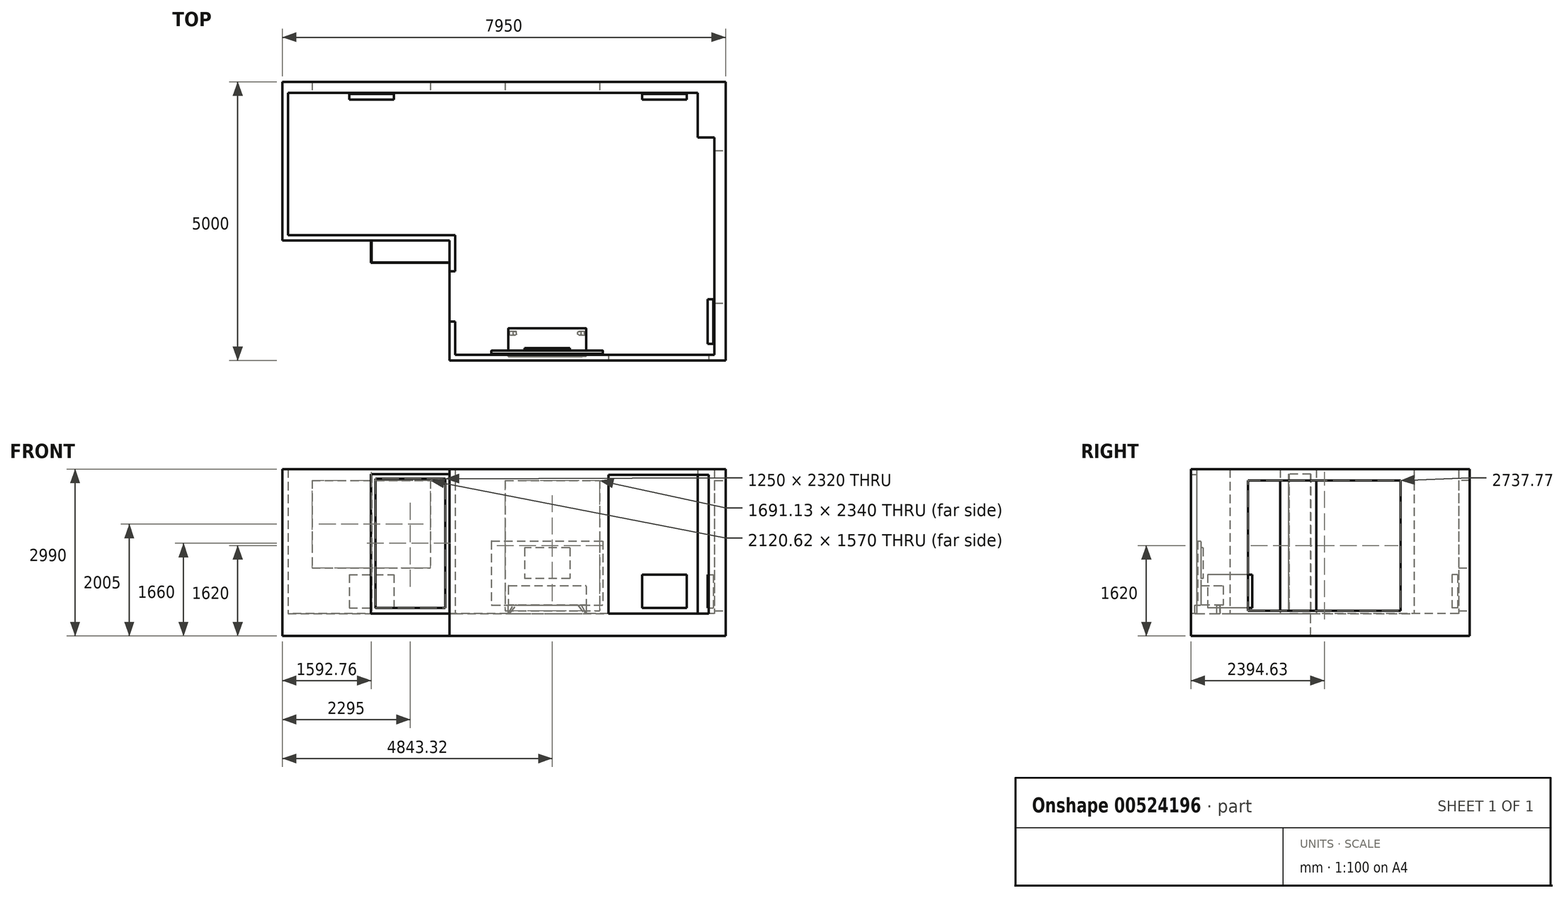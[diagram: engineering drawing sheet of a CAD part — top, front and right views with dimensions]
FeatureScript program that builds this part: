
annotation { "Feature Type Name" : "Feature", "Feature Type Description" : "" }
export const myFeature = defineFeature(function(context is Context, id is Id, definition is map)
    precondition{}
    {
        {
            var Q0;
            Q0=qCreatedBy(makeId("Top.planeOp"),FACE);
            var sketch = newSketch(context, id + "F0", { "sketchPlane" : qUnion([Q0])});
            skLineSegment(sketch, "E0.bottom", {"start": v(0, 0) * mm, "end": v(-4650, 0) * mm});
            skLineSegment(sketch, "E0.left", {"start": v(0, 0) * mm, "end": v(0, 3900) * mm});
            skLineSegment(sketch, "E0.right", {"start": v(-4650, 0) * mm, "end": v(-4650, 2150) * mm});
            skLineSegment(sketch, "E1.top", {"start": v(-4650, 2150) * mm, "end": v(-7650, 2150) * mm});
            skLineSegment(sketch, "E1.right", {"start": v(-7650, 4700) * mm, "end": v(-7650, 2150) * mm});
            skLineSegment(sketch, "E2", {"start": v(-7650, 4700) * mm, "end": v(-300, 4700) * mm});
            skLineSegment(sketch, "E3.bottom", {"start": v(-7750, 4900) * mm, "end": v(200, 4900) * mm});
            skLineSegment(sketch, "E3.top", {"start": v(-4750, -100) * mm, "end": v(200, -100) * mm});
            skLineSegment(sketch, "E3.left", {"start": v(-7750, 4900) * mm, "end": v(-7750, 2050) * mm});
            skLineSegment(sketch, "E3.right", {"start": v(200, 4900) * mm, "end": v(200, -100) * mm});
            skLineSegment(sketch, "E4.top", {"start": v(-7750, 2050) * mm, "end": v(-4750, 2050) * mm});
            skLineSegment(sketch, "E4.right", {"start": v(-4750, -100) * mm, "end": v(-4750, 2050) * mm});
            skLineSegment(sketch, "E5.bottom", {"start": v(-1900, 0) * mm, "end": v(-100, 0) * mm});
            skLineSegment(sketch, "E5.top", {"start": v(-1900, -100) * mm, "end": v(-100, -100) * mm});
            skLineSegment(sketch, "E5.left", {"start": v(-1900, 0) * mm, "end": v(-1900, -100) * mm});
            skLineSegment(sketch, "E5.right", {"start": v(-100, 0) * mm, "end": v(-100, -100) * mm});
            skLineSegment(sketch, "E6.bottom", {"start": v(-4750, 1500) * mm, "end": v(-4650, 1500) * mm});
            skLineSegment(sketch, "E6.top", {"start": v(-4750, 600) * mm, "end": v(-4650, 600) * mm});
            skLineSegment(sketch, "E6.left", {"start": v(-4750, 1500) * mm, "end": v(-4750, 600) * mm});
            skLineSegment(sketch, "E6.right", {"start": v(-4650, 1500) * mm, "end": v(-4650, 600) * mm});
            skLineSegment(sketch, "E7.bottom", {"start": v(-6160, 2050) * mm, "end": v(-4750, 2050) * mm});
            skLineSegment(sketch, "E7.top", {"start": v(-6160, 1650) * mm, "end": v(-4750, 1650) * mm});
            skLineSegment(sketch, "E7.left", {"start": v(-6160, 2050) * mm, "end": v(-6160, 1650) * mm});
            skLineSegment(sketch, "E7.right", {"start": v(-4750, 2050) * mm, "end": v(-4750, 1650) * mm});
            skLineSegment(sketch, "E8.bottom", {"start": v(-6150, 2050) * mm, "end": v(-4750, 2050) * mm});
            skLineSegment(sketch, "E8.top", {"start": v(-6150, 1660) * mm, "end": v(-4750, 1660) * mm});
            skLineSegment(sketch, "E8.left", {"start": v(-6150, 2050) * mm, "end": v(-6150, 1660) * mm});
            skLineSegment(sketch, "E8.right", {"start": v(-4750, 2050) * mm, "end": v(-4750, 1660) * mm});
            skLineSegment(sketch, "E9.top", {"start": v(-300, 3900) * mm, "end": v(0, 3900) * mm});
            skLineSegment(sketch, "E9.left", {"start": v(-300, 4700) * mm, "end": v(-300, 3900) * mm});
            skPoint(sketch, "E10.orphan", {"position": v(0, 4700) * mm});
            skLineSegment(sketch, "E11.bottom", {"start": v(0, 3663.51) * mm, "end": v(200, 3663.51) * mm});
            skLineSegment(sketch, "E11.top", {"start": v(0, 925.75) * mm, "end": v(200, 925.75) * mm});
            skLineSegment(sketch, "E11.left", {"start": v(0, 3663.51) * mm, "end": v(0, 925.75) * mm});
            skLineSegment(sketch, "E11.right", {"start": v(200, 3663.51) * mm, "end": v(200, 925.75) * mm});
            skLineSegment(sketch, "E12.bottom", {"start": v(-3752.24, 4700) * mm, "end": v(-2061.12, 4700) * mm});
            skLineSegment(sketch, "E12.top", {"start": v(-3752.24, 4900) * mm, "end": v(-2061.12, 4900) * mm});
            skLineSegment(sketch, "E12.left", {"start": v(-3752.24, 4700) * mm, "end": v(-3752.24, 4900) * mm});
            skLineSegment(sketch, "E12.right", {"start": v(-2061.12, 4700) * mm, "end": v(-2061.12, 4900) * mm});
            skLineSegment(sketch, "E13.bottom", {"start": v(-7217.55, 4700) * mm, "end": v(-5096.93, 4700) * mm});
            skLineSegment(sketch, "E13.top", {"start": v(-7217.55, 4900) * mm, "end": v(-5096.93, 4900) * mm});
            skLineSegment(sketch, "E13.left", {"start": v(-7217.55, 4700) * mm, "end": v(-7217.55, 4900) * mm});
            skLineSegment(sketch, "E13.right", {"start": v(-5096.93, 4700) * mm, "end": v(-5096.93, 4900) * mm});
            skSolve(sketch);
        }
        {
            var Q0;
            {var subQ7=sQuery(id+"F0.wireOp",EDGE,"E1.top");Q0=makeQuery(id+"F0.imprint","IMPRINT",FACE,{"disambiguationData":[TD([[makeQuery(id+"F0.imprint","IMPRINT",EDGE,{"derivedFrom":subQ7}),1.0]])]});}
            var Q1;
            {var subQ0=sQuery(id+"F0.wireOp",EDGE,"E1.top");Q1=makeQuery(id+"F0.imprint","IMPRINT",FACE,{"disambiguationData":[TD([[makeQuery(id+"F0.imprint","IMPRINT",EDGE,{"derivedFrom":subQ0}),-1.0]])]});}
            var Q2;
            {var subQ2=sQuery(id+"F0.wireOp",EDGE,"E6.bottom");Q2=makeQuery(id+"F0.imprint","IMPRINT",FACE,{"disambiguationData":[TD([[makeQuery(id+"F0.imprint","IMPRINT",EDGE,{"derivedFrom":subQ2}),-1.0]])]});}
            var Q3;
            {var subQ4=sQuery(id+"F0.wireOp",EDGE,"E5.left");Q3=makeQuery(id+"F0.imprint","IMPRINT",FACE,{"disambiguationData":[TD([[makeQuery(id+"F0.imprint","IMPRINT",EDGE,{"derivedFrom":subQ4}),-1.0]])]});}
            var Q4;
            {var subQ0=sQuery(id+"F0.wireOp",EDGE,"E12.left");Q4=makeQuery(id+"F0.imprint","IMPRINT",FACE,{"disambiguationData":[TD([[makeQuery(id+"F0.imprint","IMPRINT",EDGE,{"derivedFrom":subQ0}),-1.0]])]});}
            var Q5;
            {var subQ5=sQuery(id+"F0.wireOp",EDGE,"E9.top");Q5=makeQuery(id+"F0.imprint","IMPRINT",FACE,{"disambiguationData":[TD([[makeQuery(id+"F0.imprint","IMPRINT",EDGE,{"derivedFrom":subQ5}),1.0]])]});}
            var Q6;
            {var subQ0=sQuery(id+"F0.wireOp",EDGE,"E13.left");Q6=makeQuery(id+"F0.imprint","IMPRINT",FACE,{"disambiguationData":[TD([[makeQuery(id+"F0.imprint","IMPRINT",EDGE,{"derivedFrom":subQ0}),-1.0]])]});}
            var Q7;
            {var subQ0=sQuery(id+"F0.wireOp",EDGE,"E12.left");Q7=makeQuery(id+"F0.imprint","IMPRINT",FACE,{"disambiguationData":[TD([[makeQuery(id+"F0.imprint","IMPRINT",EDGE,{"derivedFrom":subQ0}),1.0]])]});}
            var Q8;
            {var subQ2=sQuery(id+"F0.wireOp",EDGE,"E11.bottom");Q8=makeQuery(id+"F0.imprint","IMPRINT",FACE,{"disambiguationData":[TD([[makeQuery(id+"F0.imprint","IMPRINT",EDGE,{"derivedFrom":subQ2}),-1.0]])]});}
            var Q9;
            {var subQ3=sQuery(id+"F0.wireOp",EDGE,"E5.right");Q9=makeQuery(id+"F0.imprint","IMPRINT",FACE,{"disambiguationData":[TD([[makeQuery(id+"F0.imprint","IMPRINT",EDGE,{"derivedFrom":subQ3}),1.0]])]});}
            var Q10;
            {var subQ0=sQuery(id+"F0.wireOp",EDGE,"E5.left");Q10=makeQuery(id+"F0.imprint","IMPRINT",FACE,{"disambiguationData":[TD([[makeQuery(id+"F0.imprint","IMPRINT",EDGE,{"derivedFrom":subQ0}),1.0]])]});}
            extrude(context, id + "F1", {"entities" : qUnion([Q0, Q1, Q2, Q3, Q4, Q5, Q6, Q7, Q8, Q9, Q10]), "oppositeDirection" : true, "depth" : 400 * mm, "offsetDistance" : 25 * mm});
        }
        {
            var Q0;
            {var subQ7=sQuery(id+"F0.wireOp",EDGE,"E1.top");Q0=makeQuery(id+"F0.imprint","IMPRINT",FACE,{"disambiguationData":[TD([[makeQuery(id+"F0.imprint","IMPRINT",EDGE,{"derivedFrom":subQ7}),1.0]])]});}
            var Q1;
            {var subQ0=sQuery(id+"F0.wireOp",EDGE,"E12.left");Q1=makeQuery(id+"F0.imprint","IMPRINT",FACE,{"disambiguationData":[TD([[makeQuery(id+"F0.imprint","IMPRINT",EDGE,{"derivedFrom":subQ0}),1.0]])]});}
            var Q2;
            {var subQ5=sQuery(id+"F0.wireOp",EDGE,"E9.top");Q2=makeQuery(id+"F0.imprint","IMPRINT",FACE,{"disambiguationData":[TD([[makeQuery(id+"F0.imprint","IMPRINT",EDGE,{"derivedFrom":subQ5}),1.0]])]});}
            var Q3;
            {var subQ3=sQuery(id+"F0.wireOp",EDGE,"E5.right");Q3=makeQuery(id+"F0.imprint","IMPRINT",FACE,{"disambiguationData":[TD([[makeQuery(id+"F0.imprint","IMPRINT",EDGE,{"derivedFrom":subQ3}),1.0]])]});}
            var Q4;
            {var subQ4=sQuery(id+"F0.wireOp",EDGE,"E5.left");Q4=makeQuery(id+"F0.imprint","IMPRINT",FACE,{"disambiguationData":[TD([[makeQuery(id+"F0.imprint","IMPRINT",EDGE,{"derivedFrom":subQ4}),-1.0]])]});}
            extrude(context, id + "F2", {"entities" : qUnion([Q0, Q1, Q2, Q3, Q4]), "operationType" : NewBodyOperationType.ADD, "depth" : 2590 * mm, "offsetDistance" : 25 * mm});
        }
        {
            var Q0;
            {var subQ0=sQuery(id+"F0.wireOp",EDGE,"E12.left");Q0=makeQuery(id+"F0.imprint","IMPRINT",FACE,{"disambiguationData":[TD([[makeQuery(id+"F0.imprint","IMPRINT",EDGE,{"derivedFrom":subQ0}),-1.0]])]});}
            var Q1;
            {var subQ2=sQuery(id+"F0.wireOp",EDGE,"E11.bottom");Q1=makeQuery(id+"F0.imprint","IMPRINT",FACE,{"disambiguationData":[TD([[makeQuery(id+"F0.imprint","IMPRINT",EDGE,{"derivedFrom":subQ2}),-1.0]])]});}
            extrude(context, id + "F3", {"entities" : qUnion([Q0, Q1]), "operationType" : NewBodyOperationType.ADD, "depth" : 50 * mm, "offsetDistance" : 25 * mm});
        }
        {
            var Q0;
            {var subQ0=sQuery(id+"F0.wireOp",EDGE,"E13.left");Q0=makeQuery(id+"F0.imprint","IMPRINT",FACE,{"disambiguationData":[TD([[makeQuery(id+"F0.imprint","IMPRINT",EDGE,{"derivedFrom":subQ0}),-1.0]])]});}
            extrude(context, id + "F4", {"entities" : qUnion([Q0]), "operationType" : NewBodyOperationType.ADD, "depth" : 820 * mm, "offsetDistance" : 25 * mm});
        }
        {
            var Q0;
            {var subQ3=sQuery(id+"F0.wireOp",EDGE,"E7.top");Q0=makeQuery(id+"F0.imprint","IMPRINT",FACE,{"disambiguationData":[TD([[makeQuery(id+"F0.imprint","IMPRINT",EDGE,{"derivedFrom":subQ3}),1.0]])]});}
            extrude(context, id + "F5", {"entities" : qUnion([Q0]), "operationType" : NewBodyOperationType.ADD, "depth" : 2500 * mm, "offsetDistance" : 25 * mm});
        }
        {
            var Q0;
            Q0=makeQuery(id+"F5.opExtrude","SWEPT_FACE",FACE,{"disambiguationData":[OSD([sQuery(id+"F0.wireOp",EDGE,"E7.top")])]});
            var sketch = newSketch(context, id + "F6", { "sketchPlane" : qUnion([Q0])});
            skLineSegment(sketch, "E14.0.0", {"start": v(-6160, 0) * mm, "end": v(-4750, 0) * mm});
            skLineSegment(sketch, "E14.0.1", {"start": v(-4750, 0) * mm, "end": v(-4750, 2500) * mm});
            skLineSegment(sketch, "E14.0.2", {"start": v(-4750, 2500) * mm, "end": v(-6160, 2500) * mm});
            skLineSegment(sketch, "E14.0.3", {"start": v(-6160, 2500) * mm, "end": v(-6160, 0) * mm});
            skLineSegment(sketch, "E15.bottom", {"start": v(-6080, 2420) * mm, "end": v(-4830, 2420) * mm});
            skLineSegment(sketch, "E15.top", {"start": v(-6080, 100) * mm, "end": v(-4830, 100) * mm});
            skLineSegment(sketch, "E15.left", {"start": v(-6080, 2420) * mm, "end": v(-6080, 100) * mm});
            skLineSegment(sketch, "E15.right", {"start": v(-4830, 2420) * mm, "end": v(-4830, 100) * mm});
            skSolve(sketch);
        }
        {
            var Q0;
            Q0=makeQuery(id+"F6.imprint","IMPRINT",FACE,{"disambiguationData":[TD([[makeQuery(id+"F6.imprint","IMPRINT",EDGE,{"derivedFrom":sQuery(id+"F6.wireOp",EDGE,"E15.bottom")}),-1.0]])]});
            extrude(context, id + "F7", {"entities" : qUnion([Q0]), "operationType" : NewBodyOperationType.REMOVE, "oppositeDirection" : true, "depth" : 25 * mm, "offsetDistance" : 25 * mm});
        }
        {
            var Q0;
            {var subQ0=sQuery(id+"F0.wireOp",EDGE,"E2");Q0=makeQuery(id+"F4.boolean.opBoolean","MERGE",FACE,{"derivedFrom":[makeQuery(id+"F2.opExtrude","SWEPT_FACE",FACE,{"disambiguationData":[OSD([subQ0]),TDD([makeQuery(id+"F0.imprint","IMPRINT",EDGE,{"disambiguationData":[TD([[makeQuery(id+"F0.imprint","INTERSECT",VERTEX,{"derivedFrom":[sQuery(id+"F0.wireOp",EDGE,"E1.right"),subQ0]}),-1.0]])],"derivedFrom":subQ0})])]}),makeQuery(id+"F3.boolean.opBoolean","MERGE",FACE,{"derivedFrom":[makeQuery(id+"F2.opExtrude","SWEPT_FACE",FACE,{"disambiguationData":[OSD([subQ0]),TDD([makeQuery(id+"F0.imprint","IMPRINT",EDGE,{"disambiguationData":[TD([[makeQuery(id+"F0.imprint","INTERSECT",VERTEX,{"derivedFrom":[subQ0,sQuery(id+"F0.wireOp",EDGE,"E9.left")]}),1.0]])],"derivedFrom":subQ0})])]}),makeQuery(id+"F2.opExtrude","SWEPT_FACE",FACE,{"disambiguationData":[OSD([subQ0]),TDD([makeQuery(id+"F0.imprint","IMPRINT",EDGE,{"disambiguationData":[TD([[makeQuery(id+"F0.imprint","INTERSECT",VERTEX,{"derivedFrom":[subQ0,sQuery(id+"F0.wireOp",EDGE,"E12.left")]}),1.0]])],"derivedFrom":subQ0})])]}),makeQuery(id+"F3.opExtrude","SWEPT_FACE",FACE,{"disambiguationData":[OSD([subQ0])]})]}),makeQuery(id+"F4.opExtrude","SWEPT_FACE",FACE,{"disambiguationData":[OSD([subQ0])]})]});}
            var sketch = newSketch(context, id + "F8", { "sketchPlane" : qUnion([Q0])});
            skLineSegment(sketch, "E16.0.0", {"start": v(-7650, 0) * mm, "end": v(-300, 0) * mm});
            skLineSegment(sketch, "E16.0.1", {"start": v(-300, 0) * mm, "end": v(-300, 2590) * mm});
            skLineSegment(sketch, "E16.0.2", {"start": v(-300, 2590) * mm, "end": v(-2061.12, 2590) * mm});
            skLineSegment(sketch, "E16.0.3", {"start": v(-2061.12, 2590) * mm, "end": v(-2061.12, 50) * mm});
            skLineSegment(sketch, "E16.0.4", {"start": v(-2061.12, 50) * mm, "end": v(-3752.24, 50) * mm});
            skLineSegment(sketch, "E16.0.5", {"start": v(-3752.24, 50) * mm, "end": v(-3752.24, 2590) * mm});
            skLineSegment(sketch, "E16.0.6", {"start": v(-3752.24, 2590) * mm, "end": v(-5096.93, 2590) * mm});
            skLineSegment(sketch, "E16.0.7", {"start": v(-5096.93, 2590) * mm, "end": v(-5096.93, 820) * mm});
            skLineSegment(sketch, "E16.0.8", {"start": v(-5096.93, 820) * mm, "end": v(-7217.55, 820) * mm});
            skLineSegment(sketch, "E16.0.9", {"start": v(-7217.55, 820) * mm, "end": v(-7217.55, 2590) * mm});
            skLineSegment(sketch, "E16.0.10", {"start": v(-7217.55, 2590) * mm, "end": v(-7650, 2590) * mm});
            skLineSegment(sketch, "E16.0.11", {"start": v(-7650, 2590) * mm, "end": v(-7650, 0) * mm});
            skLineSegment(sketch, "E17.bottom", {"start": v(-7217.55, 2590) * mm, "end": v(-5096.93, 2590) * mm});
            skLineSegment(sketch, "E17.top", {"start": v(-7217.55, 2390) * mm, "end": v(-5096.93, 2390) * mm});
            skLineSegment(sketch, "E17.left", {"start": v(-7217.55, 2590) * mm, "end": v(-7217.55, 2390) * mm});
            skLineSegment(sketch, "E17.right", {"start": v(-5096.93, 2590) * mm, "end": v(-5096.93, 2390) * mm});
            skLineSegment(sketch, "E18.bottom", {"start": v(-3752.24, 2590) * mm, "end": v(-2061.12, 2590) * mm});
            skLineSegment(sketch, "E18.top", {"start": v(-3752.24, 2390) * mm, "end": v(-2061.12, 2390) * mm});
            skLineSegment(sketch, "E18.left", {"start": v(-3752.24, 2590) * mm, "end": v(-3752.24, 2390) * mm});
            skLineSegment(sketch, "E18.right", {"start": v(-2061.12, 2590) * mm, "end": v(-2061.12, 2390) * mm});
            skSolve(sketch);
        }
        {
            var Q0;
            {var subQ0=sQuery(id+"F8.wireOp",EDGE,"E17.bottom");Q0=makeQuery(id+"F8.imprint","IMPRINT",FACE,{"disambiguationData":[TD([[makeQuery(id+"F8.imprint","IMPRINT",EDGE,{"derivedFrom":subQ0}),-1.0]])]});}
            var Q1;
            {var subQ0=sQuery(id+"F8.wireOp",EDGE,"E18.bottom");Q1=makeQuery(id+"F8.imprint","IMPRINT",FACE,{"disambiguationData":[TD([[makeQuery(id+"F8.imprint","IMPRINT",EDGE,{"derivedFrom":subQ0}),-1.0]])]});}
            extrude(context, id + "F9", {"entities" : qUnion([Q0, Q1]), "operationType" : NewBodyOperationType.ADD, "oppositeDirection" : true, "depth" : 200 * mm, "offsetDistance" : 25 * mm});
        }
        {
            var Q0;
            {var subQ0=sQuery(id+"F0.wireOp",EDGE,"E3.top");Q0=makeQuery(id+"F2.boolean.opBoolean","MERGE",FACE,{"derivedFrom":[makeQuery(id+"F1.opExtrude","SWEPT_FACE",FACE,{"disambiguationData":[OSD([subQ0])]}),makeQuery(id+"F2.opExtrude","SWEPT_FACE",FACE,{"disambiguationData":[OSD([subQ0]),TDD([makeQuery(id+"F0.imprint","IMPRINT",EDGE,{"disambiguationData":[TD([[makeQuery(id+"F0.imprint","INTERSECT",VERTEX,{"derivedFrom":[subQ0,sQuery(id+"F0.wireOp",EDGE,"E4.right")]}),-1.0]])],"derivedFrom":subQ0})])]}),makeQuery(id+"F2.opExtrude","SWEPT_FACE",FACE,{"disambiguationData":[OSD([subQ0]),TDD([makeQuery(id+"F0.imprint","IMPRINT",EDGE,{"disambiguationData":[TD([[makeQuery(id+"F0.imprint","INTERSECT",VERTEX,{"derivedFrom":[subQ0,sQuery(id+"F0.wireOp",EDGE,"E3.right")]}),1.0]])],"derivedFrom":subQ0})])]})]});}
            var sketch = newSketch(context, id + "F10", { "sketchPlane" : qUnion([Q0])});
            skLineSegment(sketch, "E19.bottom", {"start": v(-1900, 2590) * mm, "end": v(-100, 2590) * mm});
            skLineSegment(sketch, "E19.top", {"start": v(-1900, 2490) * mm, "end": v(-100, 2490) * mm});
            skLineSegment(sketch, "E19.left", {"start": v(-1900, 2590) * mm, "end": v(-1900, 2490) * mm});
            skLineSegment(sketch, "E19.right", {"start": v(-100, 2590) * mm, "end": v(-100, 2490) * mm});
            skSolve(sketch);
        }
        {
            var Q0;
            Q0 = qSketchRegion(id + "F10", true);
            extrude(context, id + "F11", {"entities" : qUnion([Q0]), "operationType" : NewBodyOperationType.ADD, "oppositeDirection" : true, "depth" : 100 * mm, "offsetDistance" : 25 * mm});
        }
        {
            var Q0;
            {var subQ0=sQuery(id+"F0.wireOp",EDGE,"E3.right");Q0=makeQuery(id+"F3.boolean.opBoolean","MERGE",FACE,{"derivedFrom":[makeQuery(id+"F2.boolean.opBoolean","MERGE",FACE,{"derivedFrom":[makeQuery(id+"F1.opExtrude","SWEPT_FACE",FACE,{"disambiguationData":[OSD([subQ0])]}),makeQuery(id+"F2.opExtrude","SWEPT_FACE",FACE,{"disambiguationData":[OSD([subQ0]),TDD([makeQuery(id+"F0.imprint","IMPRINT",EDGE,{"disambiguationData":[TD([[makeQuery(id+"F0.imprint","INTERSECT",VERTEX,{"derivedFrom":[subQ0,sQuery(id+"F0.wireOp",EDGE,"E11.bottom")]}),1.0]])],"derivedFrom":subQ0})])]}),makeQuery(id+"F2.opExtrude","SWEPT_FACE",FACE,{"disambiguationData":[OSD([subQ0]),TDD([makeQuery(id+"F0.imprint","IMPRINT",EDGE,{"disambiguationData":[TD([[makeQuery(id+"F0.imprint","INTERSECT",VERTEX,{"derivedFrom":[sQuery(id+"F0.wireOp",EDGE,"E3.top"),subQ0]}),1.0]])],"derivedFrom":subQ0})])]})]}),makeQuery(id+"F3.opExtrude","SWEPT_FACE",FACE,{"disambiguationData":[OSD([subQ0])]})]});}
            var sketch = newSketch(context, id + "F12", { "sketchPlane" : qUnion([Q0])});
            skLineSegment(sketch, "E20.0.0", {"start": v(4900, -400) * mm, "end": v(4900, 2590) * mm});
            skLineSegment(sketch, "E20.0.1", {"start": v(4900, 2590) * mm, "end": v(3663.51, 2590) * mm});
            skLineSegment(sketch, "E20.0.2", {"start": v(3663.51, 2590) * mm, "end": v(3663.51, 50) * mm});
            skLineSegment(sketch, "E20.0.3", {"start": v(3663.51, 50) * mm, "end": v(925.75, 50) * mm});
            skLineSegment(sketch, "E20.0.4", {"start": v(925.75, 50) * mm, "end": v(925.75, 2590) * mm});
            skLineSegment(sketch, "E20.0.5", {"start": v(925.75, 2590) * mm, "end": v(-100, 2590) * mm});
            skLineSegment(sketch, "E20.0.6", {"start": v(-100, 2590) * mm, "end": v(-100, -400) * mm});
            skLineSegment(sketch, "E20.0.7", {"start": v(-100, -400) * mm, "end": v(4900, -400) * mm});
            skLineSegment(sketch, "E21.bottom", {"start": v(925.75, 2590) * mm, "end": v(3663.51, 2590) * mm});
            skLineSegment(sketch, "E21.top", {"start": v(925.75, 2390) * mm, "end": v(3663.51, 2390) * mm});
            skLineSegment(sketch, "E21.left", {"start": v(925.75, 2590) * mm, "end": v(925.75, 2390) * mm});
            skLineSegment(sketch, "E21.right", {"start": v(3663.51, 2590) * mm, "end": v(3663.51, 2390) * mm});
            skSolve(sketch);
        }
        {
            var Q0;
            {var subQ0=sQuery(id+"F12.wireOp",EDGE,"E21.bottom");Q0=qUnion([makeQuery(id+"F12.imprint","IMPRINT",FACE,{"disambiguationData":[TD([[makeQuery(id+"F12.imprint","IMPRINT",EDGE,{"derivedFrom":sQuery(id+"F12.wireOp",EDGE,"E20.0.0")}),1.0]])]}),makeQuery(id+"F12.imprint","IMPRINT",FACE,{"disambiguationData":[TD([[makeQuery(id+"F12.imprint","IMPRINT",EDGE,{"derivedFrom":subQ0}),-1.0]])]})]);}
            extrude(context, id + "F13", {"entities" : qUnion([Q0]), "operationType" : NewBodyOperationType.ADD, "oppositeDirection" : true, "depth" : 200 * mm, "offsetDistance" : 25 * mm});
        }
        {
            var Q0;
            Q0=makeQuery(id+"F1.opExtrude","CAP_FACE",FACE,{"disambiguationData":[OSD([sQuery(id+"F0.wireOp",EDGE,"E3.bottom"),sQuery(id+"F0.wireOp",EDGE,"E3.top"),sQuery(id+"F0.wireOp",EDGE,"E3.left"),sQuery(id+"F0.wireOp",EDGE,"E3.right"),sQuery(id+"F0.wireOp",EDGE,"E4.top"),sQuery(id+"F0.wireOp",EDGE,"E4.right")])],"isStart":true});
            var sketch = newSketch(context, id + "F14", { "sketchPlane" : qUnion([Q0])});
            skLineSegment(sketch, "E22.0", {"start": v(-7650, 4700) * mm, "end": v(-300, 4700) * mm});
            skLineSegment(sketch, "E23.0", {"start": v(0, 0) * mm, "end": v(0, 3900) * mm});
            skLineSegment(sketch, "E24.bottom", {"start": v(-6550, 4680) * mm, "end": v(-5750, 4680) * mm});
            skLineSegment(sketch, "E24.top", {"start": v(-6550, 4580) * mm, "end": v(-5750, 4580) * mm});
            skLineSegment(sketch, "E24.left", {"start": v(-6550, 4680) * mm, "end": v(-6550, 4580) * mm});
            skLineSegment(sketch, "E24.right", {"start": v(-5750, 4680) * mm, "end": v(-5750, 4580) * mm});
            skLineSegment(sketch, "E25.bottom", {"start": v(-1300, 4680) * mm, "end": v(-500, 4680) * mm});
            skLineSegment(sketch, "E25.top", {"start": v(-1300, 4580) * mm, "end": v(-500, 4580) * mm});
            skLineSegment(sketch, "E25.left", {"start": v(-1300, 4680) * mm, "end": v(-1300, 4580) * mm});
            skLineSegment(sketch, "E25.right", {"start": v(-500, 4680) * mm, "end": v(-500, 4580) * mm});
            skLineSegment(sketch, "E26.bottom", {"start": v(-120, 1000) * mm, "end": v(-20, 1000) * mm});
            skLineSegment(sketch, "E26.top", {"start": v(-120, 200) * mm, "end": v(-20, 200) * mm});
            skLineSegment(sketch, "E26.left", {"start": v(-120, 1000) * mm, "end": v(-120, 200) * mm});
            skLineSegment(sketch, "E26.right", {"start": v(-20, 1000) * mm, "end": v(-20, 200) * mm});
            skSolve(sketch);
        }
        {
            var Q0;
            Q0 = qSketchRegion(id + "F14", true);
            extrude(context, id + "F15", {"entities" : qUnion([Q0]), "depth" : 700 * mm, "offsetDistance" : 25 * mm});
        }
        {
            var Q0;
            Q0=makeQuery(id+"F15.opExtrude","CAP_FACE",FACE,{"disambiguationData":[OSD([sQuery(id+"F14.wireOp",EDGE,"E24.bottom"),sQuery(id+"F14.wireOp",EDGE,"E24.top"),sQuery(id+"F14.wireOp",EDGE,"E24.left"),sQuery(id+"F14.wireOp",EDGE,"E24.right")])],"isStart":true});
            var sketch = newSketch(context, id + "F16", { "sketchPlane" : qUnion([Q0])});
            skPoint(sketch, "E27.0", {"position": v(-6150, -4580) * mm});
            skLineSegment(sketch, "E28.0", {"start": v(-120, -1000) * mm, "end": v(-120, -200) * mm});
            skSolve(sketch);
        }
        {
            var Q0;
            Q0 = qSketchRegion(id + "F16", true);
            var Q1;
            Q1=makeQuery(id+"F15.opExtrude","CAP_FACE",FACE,{"disambiguationData":[OSD([sQuery(id+"F14.wireOp",EDGE,"E25.bottom"),sQuery(id+"F14.wireOp",EDGE,"E25.top"),sQuery(id+"F14.wireOp",EDGE,"E25.left"),sQuery(id+"F14.wireOp",EDGE,"E25.right")])],"isStart":true});
            var Q2;
            Q2=makeQuery(id+"F15.opExtrude","CAP_FACE",FACE,{"disambiguationData":[OSD([sQuery(id+"F14.wireOp",EDGE,"E26.bottom"),sQuery(id+"F14.wireOp",EDGE,"E26.top"),sQuery(id+"F14.wireOp",EDGE,"E26.left"),sQuery(id+"F14.wireOp",EDGE,"E26.right")])],"isStart":true});
            var Q3;
            Q3=makeQuery(id+"F16.imprint","IMPRINT",FACE,{"disambiguationData":[TD([[makeQuery(id+"F16.imprint","IMPRINT",EDGE,{"derivedFrom":makeQuery(id+"F15.opExtrude","CAP_EDGE",EDGE,{"disambiguationData":[OSD([sQuery(id+"F14.wireOp",EDGE,"E24.bottom")])],"isStart":true})}),1.0]])]});
            extrude(context, id + "F17", {"entities" : qUnion([Q0, Q1, Q2, Q3]), "operationType" : NewBodyOperationType.REMOVE, "oppositeDirection" : true, "depth" : 100 * mm, "offsetDistance" : 25 * mm});
        }
        {
            var Q0;
            Q0=makeQuery(id+"F1.opExtrude","CAP_FACE",FACE,{"disambiguationData":[OSD([sQuery(id+"F0.wireOp",EDGE,"E3.bottom"),sQuery(id+"F0.wireOp",EDGE,"E3.top"),sQuery(id+"F0.wireOp",EDGE,"E3.left"),sQuery(id+"F0.wireOp",EDGE,"E3.right"),sQuery(id+"F0.wireOp",EDGE,"E4.top"),sQuery(id+"F0.wireOp",EDGE,"E4.right")])],"isStart":true});
            var sketch = newSketch(context, id + "F18", { "sketchPlane" : qUnion([Q0])});
            skLineSegment(sketch, "E29.0.0", {"start": v(-300, 4700) * mm, "end": v(-7650, 4700) * mm});
            skLineSegment(sketch, "E29.0.1", {"start": v(-7650, 4700) * mm, "end": v(-7650, 2150) * mm});
            skLineSegment(sketch, "E29.0.2", {"start": v(-7650, 2150) * mm, "end": v(-4650, 2150) * mm});
            skLineSegment(sketch, "E29.0.3", {"start": v(-4650, 2150) * mm, "end": v(-4650, 1500) * mm});
            skLineSegment(sketch, "E29.0.4", {"start": v(-4650, 1500) * mm, "end": v(-4750, 1500) * mm});
            skLineSegment(sketch, "E29.0.5", {"start": v(-4750, 1500) * mm, "end": v(-4750, 600) * mm});
            skLineSegment(sketch, "E29.0.6", {"start": v(-4750, 600) * mm, "end": v(-4650, 600) * mm});
            skLineSegment(sketch, "E29.0.7", {"start": v(-4650, 600) * mm, "end": v(-4650, 0) * mm});
            skLineSegment(sketch, "E29.0.8", {"start": v(-4650, 0) * mm, "end": v(-1900, 0) * mm});
            skLineSegment(sketch, "E29.0.9", {"start": v(-1900, 0) * mm, "end": v(-1900, -100) * mm});
            skLineSegment(sketch, "E29.0.10", {"start": v(-1900, -100) * mm, "end": v(-100, -100) * mm});
            skLineSegment(sketch, "E29.0.11", {"start": v(-100, -100) * mm, "end": v(-100, 0) * mm});
            skLineSegment(sketch, "E29.0.12", {"start": v(-100, 0) * mm, "end": v(0, 0) * mm});
            skLineSegment(sketch, "E29.0.13", {"start": v(0, 0) * mm, "end": v(0, 3900) * mm});
            skLineSegment(sketch, "E29.0.14", {"start": v(0, 3900) * mm, "end": v(-300, 3900) * mm});
            skLineSegment(sketch, "E29.0.15", {"start": v(-300, 3900) * mm, "end": v(-300, 4700) * mm});
            skLineSegment(sketch, "E30.bottom", {"start": v(-4000, 20) * mm, "end": v(-2000, 20) * mm});
            skLineSegment(sketch, "E30.top", {"start": v(-4000, 80) * mm, "end": v(-2000, 80) * mm});
            skLineSegment(sketch, "E30.left", {"start": v(-4000, 20) * mm, "end": v(-4000, 80) * mm});
            skLineSegment(sketch, "E30.right", {"start": v(-2000, 20) * mm, "end": v(-2000, 80) * mm});
            skLineSegment(sketch, "E31.bottom", {"start": v(-3700, 80) * mm, "end": v(-2300, 80) * mm});
            skLineSegment(sketch, "E31.top", {"start": v(-3700, 480) * mm, "end": v(-2300, 480) * mm});
            skLineSegment(sketch, "E31.left", {"start": v(-3700, 80) * mm, "end": v(-3700, 480) * mm});
            skLineSegment(sketch, "E31.right", {"start": v(-2300, 80) * mm, "end": v(-2300, 480) * mm});
            skSolve(sketch);
        }
        {
            var Q0;
            Q0=makeQuery(id+"F18.imprint","IMPRINT",FACE,{"disambiguationData":[TD([[makeQuery(id+"F18.imprint","IMPRINT",EDGE,{"derivedFrom":sQuery(id+"F18.wireOp",EDGE,"E30.bottom")}),1.0]])]});
            extrude(context, id + "F19", {"entities" : qUnion([Q0]), "depth" : 1300 * mm, "offsetDistance" : 25 * mm});
        }
        {
            var Q0;
            Q0=makeQuery(id+"F18.imprint","IMPRINT",FACE,{"disambiguationData":[TD([[makeQuery(id+"F18.imprint","IMPRINT",EDGE,{"derivedFrom":sQuery(id+"F18.wireOp",EDGE,"E31.top")}),-1.0]])]});
            extrude(context, id + "F20", {"entities" : qUnion([Q0]), "depth" : 500 * mm, "offsetDistance" : 25 * mm});
        }
        {
            var Q0;
            Q0=makeQuery(id+"F19.opExtrude","SWEPT_FACE",FACE,{"disambiguationData":[OSD([sQuery(id+"F18.wireOp",EDGE,"E30.top")])]});
            var sketch = newSketch(context, id + "F21", { "sketchPlane" : qUnion([Q0])});
            skLineSegment(sketch, "E32.bottom", {"start": v(4000, 0) * mm, "end": v(2000, 0) * mm});
            skLineSegment(sketch, "E32.top", {"start": v(4000, 150) * mm, "end": v(2000, 150) * mm});
            skLineSegment(sketch, "E32.left", {"start": v(4000, 0) * mm, "end": v(4000, 150) * mm});
            skLineSegment(sketch, "E32.right", {"start": v(2000, 0) * mm, "end": v(2000, 150) * mm});
            skSolve(sketch);
        }
        {
            var Q0;
            Q0 = qSketchRegion(id + "F21", true);
            extrude(context, id + "F22", {"entities" : qUnion([Q0]), "operationType" : NewBodyOperationType.REMOVE, "oppositeDirection" : true, "depth" : 60 * mm, "offsetDistance" : 25 * mm});
        }
        {
            var Q0;
            Q0=makeQuery(id+"F20.opExtrude","SWEPT_FACE",FACE,{"disambiguationData":[OSD([sQuery(id+"F18.wireOp",EDGE,"E31.right")])]});
            var sketch = newSketch(context, id + "F23", { "sketchPlane" : qUnion([Q0])});
            skPoint(sketch, "E33.0", {"position": v(50, 150) * mm});
            skPoint(sketch, "E34.0", {"position": v(80, 150) * mm});
            skLineSegment(sketch, "E35.bottom", {"start": v(80, 150) * mm, "end": v(360, 150) * mm});
            skLineSegment(sketch, "E35.top", {"start": v(80, 0) * mm, "end": v(360, 0) * mm});
            skLineSegment(sketch, "E35.left", {"start": v(80, 150) * mm, "end": v(80, 0) * mm});
            skLineSegment(sketch, "E35.right", {"start": v(360, 150) * mm, "end": v(360, 0) * mm});
            skLineSegment(sketch, "E36.bottom", {"start": v(420, 0) * mm, "end": v(480, 0) * mm});
            skLineSegment(sketch, "E36.top", {"start": v(420, 150) * mm, "end": v(480, 150) * mm});
            skLineSegment(sketch, "E36.left", {"start": v(420, 0) * mm, "end": v(420, 150) * mm});
            skLineSegment(sketch, "E36.right", {"start": v(480, 0) * mm, "end": v(480, 150) * mm});
            skSolve(sketch);
        }
        {
            var Q0;
            Q0 = qSketchRegion(id + "F23", true);
            extrude(context, id + "F24", {"entities" : qUnion([Q0]), "operationType" : NewBodyOperationType.REMOVE, "oppositeDirection" : true, "depth" : 1500 * mm, "offsetDistance" : 25 * mm});
        }
        {
            var Q0;
            Q0=makeQuery(id+"F24.boolean.opBoolean","COPY",FACE,{"derivedFrom":makeQuery(id+"F24.opExtrude","SWEPT_FACE",FACE,{"disambiguationData":[OSD([sQuery(id+"F23.wireOp",EDGE,"E36.left")])]})});
            var sketch = newSketch(context, id + "F25", { "sketchPlane" : qUnion([Q0])});
            skLineSegment(sketch, "E37.0", {"start": v(4000, 150) * mm, "end": v(2000, 150) * mm});
            skLineSegment(sketch, "E38.bottom", {"start": v(2450, 0) * mm, "end": v(3550, 0) * mm});
            skLineSegment(sketch, "E38.top", {"start": v(2450, 150) * mm, "end": v(3550, 150) * mm});
            skLineSegment(sketch, "E39", {"start": v(2300, 0) * mm, "end": v(2390, 150) * mm});
            skLineSegment(sketch, "E40", {"start": v(2330, 0) * mm, "end": v(2450, 150) * mm});
            skLineSegment(sketch, "E41", {"start": v(3550, 150) * mm, "end": v(3670, 0) * mm});
            skLineSegment(sketch, "E42", {"start": v(3610, 150) * mm, "end": v(3700, 0) * mm});
            skSolve(sketch);
        }
        {
            var Q0;
            {var subQ2=sQuery(id+"F25.wireOp",EDGE,"E39");Q0=makeQuery(id+"F25.imprint","IMPRINT",FACE,{"disambiguationData":[TD([[makeQuery(id+"F25.imprint","IMPRINT",EDGE,{"derivedFrom":subQ2}),1.0]])]});}
            var Q1;
            {var subQ1=sQuery(id+"F25.wireOp",EDGE,"E38.bottom");Q1=makeQuery(id+"F25.imprint","IMPRINT",FACE,{"disambiguationData":[TD([[makeQuery(id+"F25.imprint","IMPRINT",EDGE,{"derivedFrom":subQ1}),-1.0]])]});}
            var Q2;
            {var subQ2=sQuery(id+"F25.wireOp",EDGE,"E42");Q2=makeQuery(id+"F25.imprint","IMPRINT",FACE,{"disambiguationData":[TD([[makeQuery(id+"F25.imprint","IMPRINT",EDGE,{"derivedFrom":subQ2}),1.0]])]});}
            extrude(context, id + "F26", {"entities" : qUnion([Q0, Q1, Q2]), "operationType" : NewBodyOperationType.REMOVE, "oppositeDirection" : true, "depth" : 450 * mm, "offsetDistance" : 25 * mm});
        }
        {
            var Q0;
            Q0=makeQuery(id+"F20.opExtrude","CAP_EDGE",EDGE,{"disambiguationData":[OSD([sQuery(id+"F18.wireOp",EDGE,"E31.top")])],"isStart":false});
            var Q1;
            Q1=makeQuery(id+"F20.opExtrude","SWEPT_EDGE",EDGE,{"disambiguationData":[OSD([sQuery(id+"F18.wireOp",EDGE,"E31.top"),sQuery(id+"F18.wireOp",EDGE,"E31.right")])]});
            var Q2;
            Q2=makeQuery(id+"F24.boolean.opBoolean","COPY",EDGE,{"derivedFrom":makeQuery(id+"F24.opExtrude","SWEPT_EDGE",EDGE,{"disambiguationData":[OSD([sQuery(id+"F18.wireOp",EDGE,"E31.top"),sQuery(id+"F18.wireOp",EDGE,"E31.right"),sQuery(id+"F23.wireOp",EDGE,"E36.top"),sQuery(id+"F23.wireOp",EDGE,"E36.right")])]})});
            var Q3;
            Q3=makeQuery(id+"F20.opExtrude","SWEPT_EDGE",EDGE,{"disambiguationData":[OSD([sQuery(id+"F18.wireOp",EDGE,"E31.top"),sQuery(id+"F18.wireOp",EDGE,"E31.left")])]});
            var Q4;
            Q4=makeQuery(id+"F20.opExtrude","CAP_EDGE",EDGE,{"disambiguationData":[OSD([sQuery(id+"F18.wireOp",EDGE,"E31.left")])],"isStart":false});
            var Q5;
            {var subQ0=sQuery(id+"F18.wireOp",EDGE,"E31.left");var subQ1=makeQuery(id+"F20.opExtrude","SWEPT_FACE",FACE,{"disambiguationData":[OSD([subQ0])]});Q5=makeQuery(id+"F26.boolean.opBoolean","MERGE",EDGE,{"derivedFrom":[makeQuery(id+"F24.boolean.opBoolean","INTERSECT",EDGE,{"derivedFrom":[subQ1,makeQuery(id+"F24.opExtrude","SWEPT_FACE",FACE,{"disambiguationData":[OSD([sQuery(id+"F23.wireOp",EDGE,"E35.bottom")])]})]}),makeQuery(id+"F24.boolean.opBoolean","INTERSECT",EDGE,{"derivedFrom":[subQ1,makeQuery(id+"F24.opExtrude","SWEPT_FACE",FACE,{"disambiguationData":[OSD([sQuery(id+"F23.wireOp",EDGE,"E36.top")])]})]})],"fromTools":[makeQuery(id+"F26.opExtrude","SWEPT_EDGE",EDGE,{"disambiguationData":[OSD([subQ0,sQuery(id+"F23.wireOp",EDGE,"E36.left"),sQuery(id+"F25.wireOp",EDGE,"E37.0")])]})]});}
            var Q6;
            Q6=makeQuery(id+"F20.opExtrude","CAP_EDGE",EDGE,{"disambiguationData":[OSD([sQuery(id+"F18.wireOp",EDGE,"E31.right")])],"isStart":false});
            var Q7;
            Q7=makeQuery(id+"F26.boolean.opBoolean","MERGE",EDGE,{"derivedFrom":[makeQuery(id+"F24.boolean.opBoolean","COPY",EDGE,{"derivedFrom":makeQuery(id+"F24.opExtrude","CAP_EDGE",EDGE,{"disambiguationData":[OSD([sQuery(id+"F23.wireOp",EDGE,"E35.bottom")])],"isStart":true})}),makeQuery(id+"F24.boolean.opBoolean","COPY",EDGE,{"derivedFrom":makeQuery(id+"F24.opExtrude","CAP_EDGE",EDGE,{"disambiguationData":[OSD([sQuery(id+"F23.wireOp",EDGE,"E36.top")])],"isStart":true})})],"fromTools":[makeQuery(id+"F26.opExtrude","SWEPT_EDGE",EDGE,{"disambiguationData":[OSD([sQuery(id+"F23.wireOp",EDGE,"E36.left"),sQuery(id+"F25.wireOp",EDGE,"E37.0")])]})]});
            fillet(context, id + "F27", {"entities" : qUnion([Q0, Q1, Q2, Q3, Q4, Q5, Q6, Q7]), "radius" : 10 * mm, "tangentPropagation" : true, "allowEdgeOverflow" : false});
        }
        {
            var Q0;
            Q0=makeQuery(id+"F26.boolean.opBoolean","COPY",EDGE,{"derivedFrom":makeQuery(id+"F26.opExtrude","CAP_EDGE",EDGE,{"disambiguationData":[OSD([sQuery(id+"F25.wireOp",EDGE,"E39")])],"isStart":true})});
            var Q1;
            Q1=makeQuery(id+"F26.boolean.opBoolean","INTERSECT",EDGE,{"derivedFrom":[makeQuery(id+"F24.boolean.opBoolean","COPY",FACE,{"derivedFrom":makeQuery(id+"F24.opExtrude","SWEPT_FACE",FACE,{"disambiguationData":[OSD([sQuery(id+"F23.wireOp",EDGE,"E35.right")])]})}),makeQuery(id+"F26.opExtrude","SWEPT_FACE",FACE,{"disambiguationData":[OSD([sQuery(id+"F25.wireOp",EDGE,"E39")])]})]});
            var Q2;
            Q2=makeQuery(id+"F26.boolean.opBoolean","COPY",EDGE,{"derivedFrom":makeQuery(id+"F26.opExtrude","CAP_EDGE",EDGE,{"disambiguationData":[OSD([sQuery(id+"F25.wireOp",EDGE,"E40")])],"isStart":true})});
            var Q3;
            Q3=makeQuery(id+"F26.boolean.opBoolean","INTERSECT",EDGE,{"derivedFrom":[makeQuery(id+"F24.boolean.opBoolean","COPY",FACE,{"derivedFrom":makeQuery(id+"F24.opExtrude","SWEPT_FACE",FACE,{"disambiguationData":[OSD([sQuery(id+"F23.wireOp",EDGE,"E35.right")])]})}),makeQuery(id+"F26.opExtrude","SWEPT_FACE",FACE,{"disambiguationData":[OSD([sQuery(id+"F25.wireOp",EDGE,"E40")])]})]});
            var Q4;
            Q4=makeQuery(id+"F26.boolean.opBoolean","COPY",EDGE,{"derivedFrom":makeQuery(id+"F26.opExtrude","CAP_EDGE",EDGE,{"disambiguationData":[OSD([sQuery(id+"F25.wireOp",EDGE,"E41")])],"isStart":true})});
            var Q5;
            Q5=makeQuery(id+"F26.boolean.opBoolean","COPY",EDGE,{"derivedFrom":makeQuery(id+"F26.opExtrude","CAP_EDGE",EDGE,{"disambiguationData":[OSD([sQuery(id+"F25.wireOp",EDGE,"E42")])],"isStart":true})});
            var Q6;
            Q6=makeQuery(id+"F26.boolean.opBoolean","INTERSECT",EDGE,{"derivedFrom":[makeQuery(id+"F24.boolean.opBoolean","COPY",FACE,{"derivedFrom":makeQuery(id+"F24.opExtrude","SWEPT_FACE",FACE,{"disambiguationData":[OSD([sQuery(id+"F23.wireOp",EDGE,"E35.right")])]})}),makeQuery(id+"F26.opExtrude","SWEPT_FACE",FACE,{"disambiguationData":[OSD([sQuery(id+"F25.wireOp",EDGE,"E42")])]})]});
            var Q7;
            Q7=makeQuery(id+"F26.boolean.opBoolean","INTERSECT",EDGE,{"derivedFrom":[makeQuery(id+"F24.boolean.opBoolean","COPY",FACE,{"derivedFrom":makeQuery(id+"F24.opExtrude","SWEPT_FACE",FACE,{"disambiguationData":[OSD([sQuery(id+"F23.wireOp",EDGE,"E35.right")])]})}),makeQuery(id+"F26.opExtrude","SWEPT_FACE",FACE,{"disambiguationData":[OSD([sQuery(id+"F25.wireOp",EDGE,"E41")])]})]});
            fillet(context, id + "F28", {"entities" : qUnion([Q0, Q1, Q2, Q3, Q4, Q5, Q6, Q7]), "radius" : 15 * mm, "tangentPropagation" : true, "allowEdgeOverflow" : false});
        }
        {
            var Q0;
            Q0=makeQuery(id+"F19.opExtrude","CAP_EDGE",EDGE,{"disambiguationData":[OSD([sQuery(id+"F18.wireOp",EDGE,"E30.top")])],"isStart":false});
            var Q1;
            Q1=makeQuery(id+"F19.opExtrude","SWEPT_EDGE",EDGE,{"disambiguationData":[OSD([sQuery(id+"F18.wireOp",EDGE,"E30.top"),sQuery(id+"F18.wireOp",EDGE,"E30.right")])]});
            var Q2;
            Q2=makeQuery(id+"F19.opExtrude","SWEPT_EDGE",EDGE,{"disambiguationData":[OSD([sQuery(id+"F18.wireOp",EDGE,"E30.top"),sQuery(id+"F18.wireOp",EDGE,"E30.left")])]});
            fillet(context, id + "F29", {"entities" : qUnion([Q0, Q1, Q2]), "radius" : 10 * mm, "tangentPropagation" : true, "allowEdgeOverflow" : false});
        }
        {
            var Q0;
            Q0=makeQuery(id+"F19.opExtrude","SWEPT_FACE",FACE,{"disambiguationData":[OSD([sQuery(id+"F18.wireOp",EDGE,"E30.top")])]});
            var sketch = newSketch(context, id + "F30", { "sketchPlane" : qUnion([Q0])});
            skLineSegment(sketch, "E43.0", {"start": v(2000, 1300) * mm, "end": v(4000, 1300) * mm});
            skLineSegment(sketch, "E44.0", {"start": v(2000, 150) * mm, "end": v(2000, 1300) * mm});
            skLineSegment(sketch, "E45.0", {"start": v(3990, 150) * mm, "end": v(2010, 150) * mm});
            skLineSegment(sketch, "E46.bottom", {"start": v(2595, 1180) * mm, "end": v(3405, 1180) * mm});
            skLineSegment(sketch, "E46.top", {"start": v(2595, 630) * mm, "end": v(3405, 630) * mm});
            skLineSegment(sketch, "E46.left", {"start": v(2595, 1180) * mm, "end": v(2595, 630) * mm});
            skLineSegment(sketch, "E46.right", {"start": v(3405, 1180) * mm, "end": v(3405, 630) * mm});
            skSolve(sketch);
        }
        {
            var Q0;
            Q0=makeQuery(id+"F30.imprint","IMPRINT",FACE,{"disambiguationData":[TD([[makeQuery(id+"F30.imprint","IMPRINT",EDGE,{"derivedFrom":sQuery(id+"F30.wireOp",EDGE,"E46.bottom")}),-1.0]])]});
            extrude(context, id + "F31", {"entities" : qUnion([Q0]), "depth" : 40 * mm, "offsetDistance" : 25 * mm});
        }
    });
